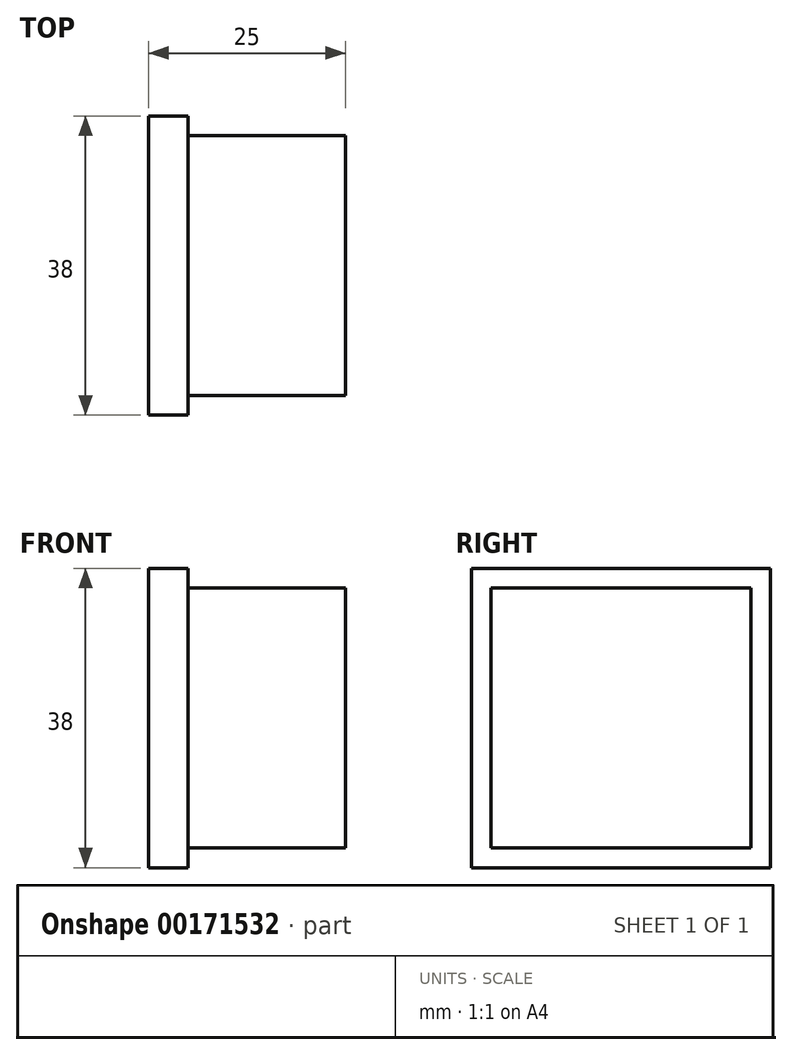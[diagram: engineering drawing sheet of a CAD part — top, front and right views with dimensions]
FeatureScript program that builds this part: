
annotation { "Feature Type Name" : "Feature", "Feature Type Description" : "" }
export const myFeature = defineFeature(function(context is Context, id is Id, definition is map)
    precondition{}
    {
        {
            var Q0;
            Q0=qCreatedBy(makeId("Right.planeOp"),FACE);
            var sketch = newSketch(context, id + "F0", { "sketchPlane" : qUnion([Q0])});
            skLineSegment(sketch, "E0.bottom", {"start": v(19, -19) * mm, "end": v(-19, -19) * mm});
            skLineSegment(sketch, "E0.top", {"start": v(19, 19) * mm, "end": v(-19, 19) * mm});
            skLineSegment(sketch, "E0.left", {"start": v(19, -19) * mm, "end": v(19, 19) * mm});
            skLineSegment(sketch, "E0.right", {"start": v(-19, -19) * mm, "end": v(-19, 19) * mm});
            skPoint(sketch, "E0.middle", {"position": v(0, 0) * mm});
            skLineSegment(sketch, "E1.bottom", {"start": v(16.5, -16.5) * mm, "end": v(-16.5, -16.5) * mm});
            skLineSegment(sketch, "E1.top", {"start": v(16.5, 16.5) * mm, "end": v(-16.5, 16.5) * mm});
            skLineSegment(sketch, "E1.left", {"start": v(16.5, -16.5) * mm, "end": v(16.5, 16.5) * mm});
            skLineSegment(sketch, "E1.right", {"start": v(-16.5, -16.5) * mm, "end": v(-16.5, 16.5) * mm});
            skSolve(sketch);
        }
        {
            var Q0;
            Q0=makeQuery(id+"F0.imprint","IMPRINT",FACE,{"disambiguationData":[TD([[makeQuery(id+"F0.imprint","IMPRINT",EDGE,{"derivedFrom":sQuery(id+"F0.wireOp",EDGE,"E1.bottom")}),-1.0]])]});
            extrude(context, id + "F1", {"entities" : qUnion([Q0]), "depth" : 20 * mm});
        }
        {
            var Q0;
            Q0=makeQuery(id+"F0.imprint","IMPRINT",FACE,{"disambiguationData":[TD([[makeQuery(id+"F0.imprint","IMPRINT",EDGE,{"derivedFrom":sQuery(id+"F0.wireOp",EDGE,"E0.bottom")}),-1.0]])]});
            var Q1;
            Q1=makeQuery(id+"F0.imprint","IMPRINT",FACE,{"disambiguationData":[TD([[makeQuery(id+"F0.imprint","IMPRINT",EDGE,{"derivedFrom":sQuery(id+"F0.wireOp",EDGE,"E1.bottom")}),-1.0]])]});
            extrude(context, id + "F2", {"entities" : qUnion([Q0, Q1]), "operationType" : NewBodyOperationType.ADD, "oppositeDirection" : true, "depth" : 5 * mm});
        }
    });
